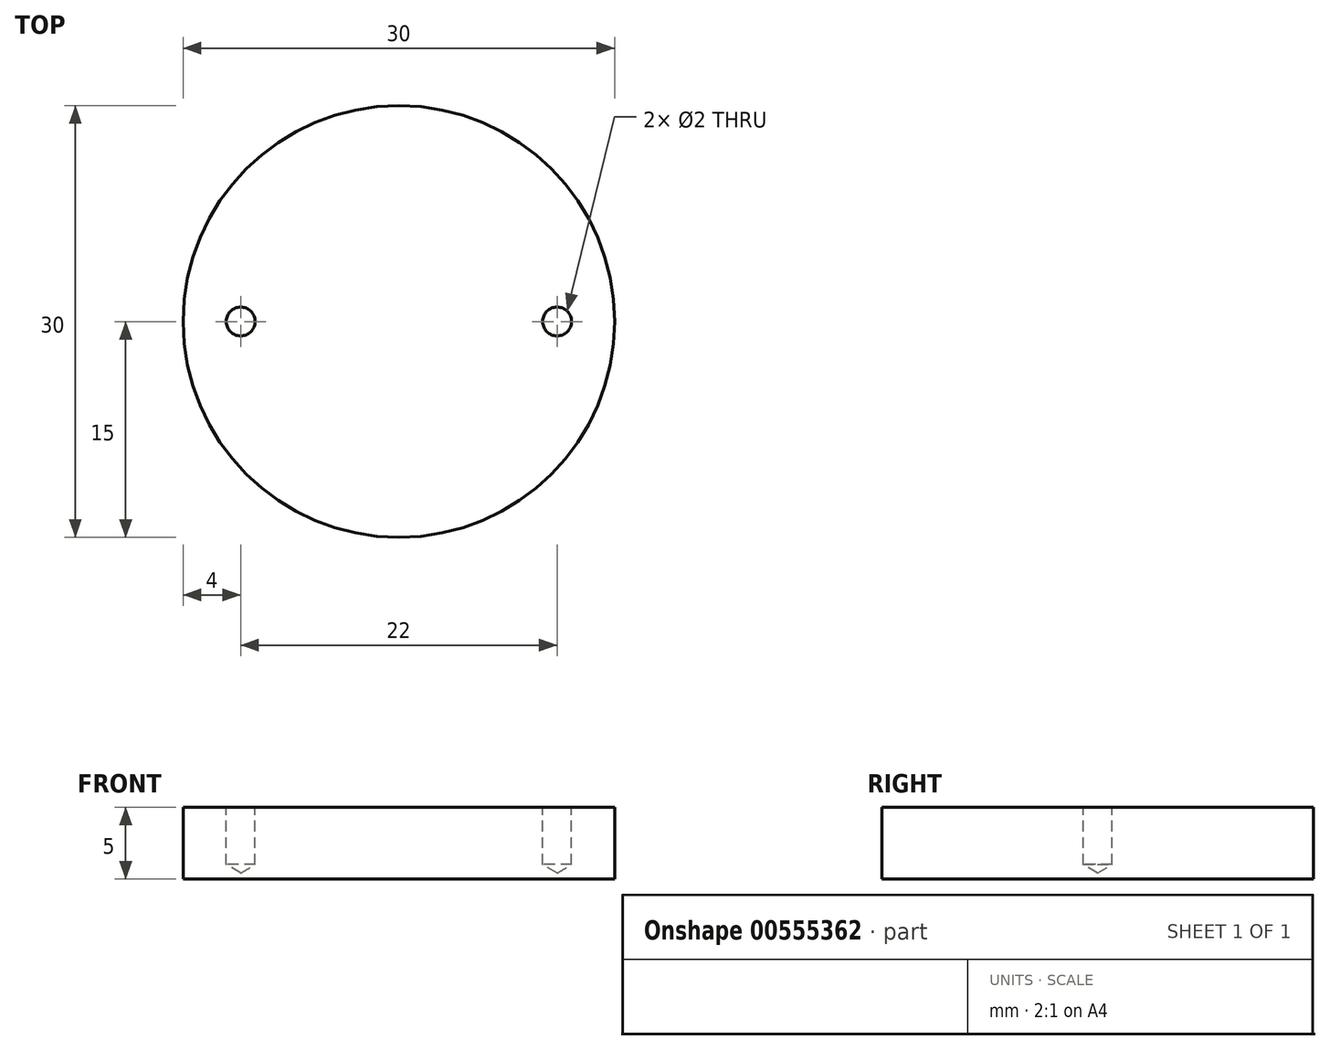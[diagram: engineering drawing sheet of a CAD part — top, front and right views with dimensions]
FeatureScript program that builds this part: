
annotation { "Feature Type Name" : "Feature", "Feature Type Description" : "" }
export const myFeature = defineFeature(function(context is Context, id is Id, definition is map)
    precondition{}
    {
        {
            var Q0;
            Q0=qCreatedBy(makeId("Top.planeOp"),FACE);
            var sketch = newSketch(context, id + "F0", { "sketchPlane" : qUnion([Q0])});
            skCircle(sketch, "E0", {"center": v(0, 0) * mm, "radius": 15 * mm});
            skSolve(sketch);
        }
        {
            var Q0;
            Q0=makeQuery(id+"F0.imprint","IMPRINT",FACE,{"disambiguationData":[TD([[makeQuery(id+"F0.imprint","IMPRINT",EDGE,{"derivedFrom":sQuery(id+"F0.wireOp",EDGE,"E0")}),1.0]])]});
            extrude(context, id + "F1", {"entities" : qUnion([Q0]), "depth" : 5 * mm, "offsetDistance" : 25 * mm});
        }
        {
            var Q0;
            Q0=makeQuery(id+"F1.opExtrude","CAP_FACE",FACE,{"disambiguationData":[OSD([sQuery(id+"F0.wireOp",EDGE,"E0")])],"isStart":false});
            var sketch = newSketch(context, id + "F2", { "sketchPlane" : qUnion([Q0])});
            skLineSegment(sketch, "E1", {"start": v(0, 0) * mm, "end": v(11, 0) * mm, "construction": true});
            skLineSegment(sketch, "E2", {"start": v(0, 0) * mm, "end": v(-11, 0) * mm, "construction": true});
            skSolve(sketch);
        }
        {
            var Q0;
            Q0=sQuery(id+"F2.wireOp",VERTEX,"E1.end");
            var Q1;
            Q1=sQuery(id+"F2.wireOp",VERTEX,"E2.end");
            var Q2;
            Q2=makeQuery(id+"F1.opExtrude","SWEPT_BODY",BODY,{"disambiguationData":[OSD([sQuery(id+"F0.wireOp",EDGE,"E0")])]});
            hole(context, id + "F3", {"style" : HoleStyle.SIMPLE, "endStyle" : HoleEndStyle.BLIND, "holeDiameter" : 2 * mm, "majorDiameter" : 5 * mm, "holeDepth" : 4 * mm, "isTappedThrough" : true, "tappedDepth" : 12 * mm, "tapClearance" : 3, "locations" : qUnion([Q0, Q1]), "scope" : qUnion([Q2])});
        }
    });
